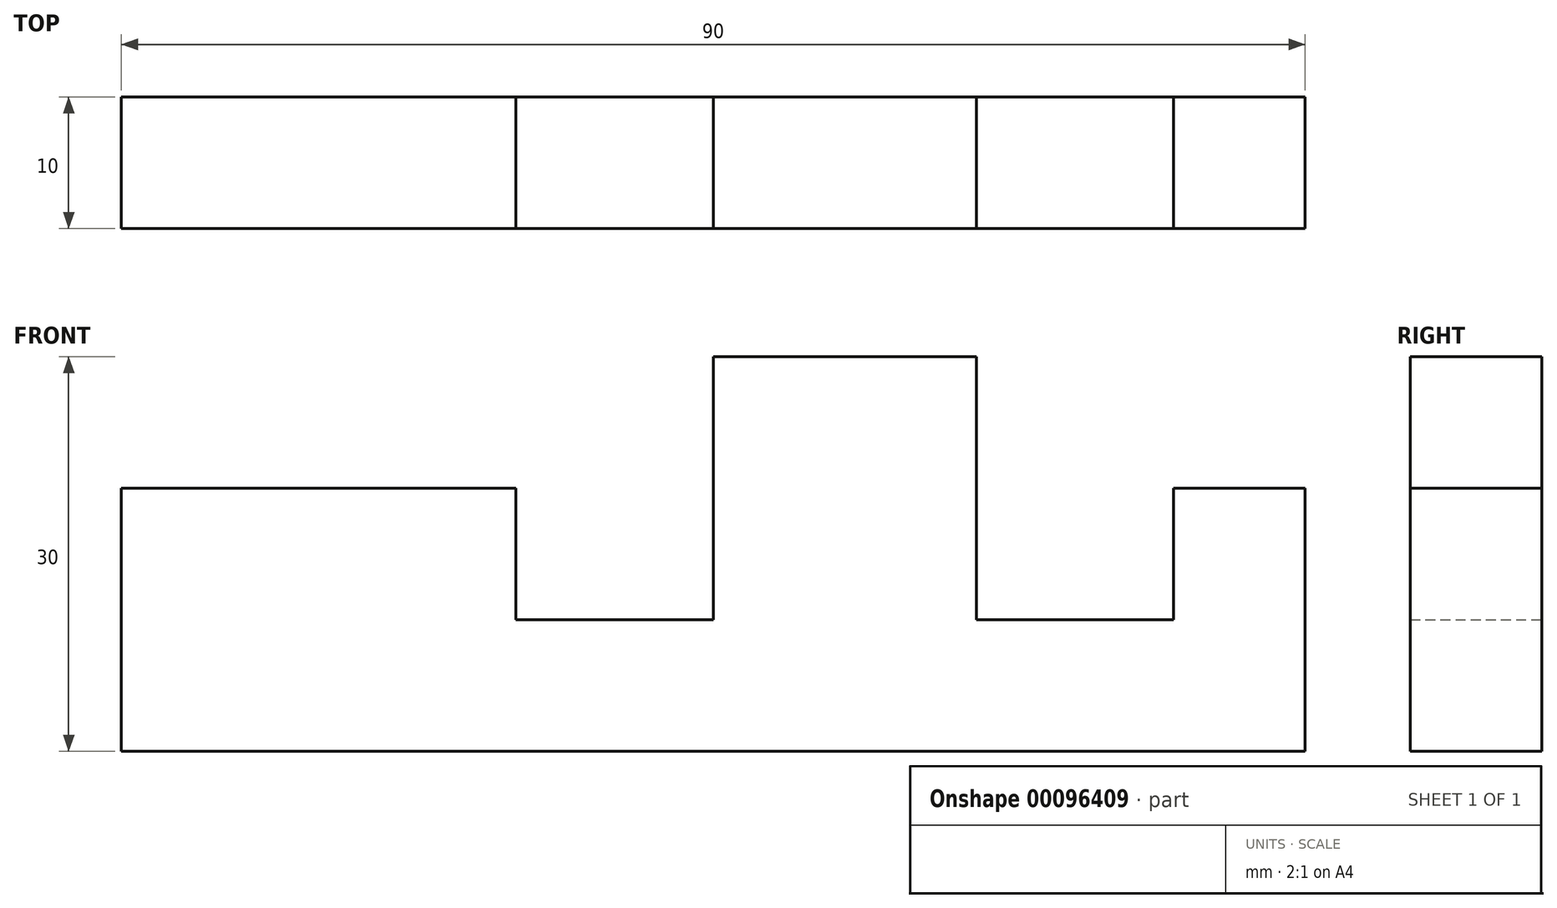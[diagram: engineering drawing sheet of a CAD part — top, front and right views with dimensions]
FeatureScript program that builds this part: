
annotation { "Feature Type Name" : "Feature", "Feature Type Description" : "" }
export const myFeature = defineFeature(function(context is Context, id is Id, definition is map)
    precondition{}
    {
        {
            var Q0;
            Q0=qCreatedBy(makeId("Front.planeOp"),FACE);
            var sketch = newSketch(context, id + "F0", { "sketchPlane" : qUnion([Q0])});
            skLineSegment(sketch, "E0", {"start": v(0, 0) * mm, "end": v(90, 0) * mm});
            skLineSegment(sketch, "E1", {"start": v(90, 0) * mm, "end": v(90, 20) * mm});
            skLineSegment(sketch, "E2", {"start": v(90, 20) * mm, "end": v(80, 20) * mm});
            skLineSegment(sketch, "E3", {"start": v(80, 20) * mm, "end": v(80, 10) * mm});
            skLineSegment(sketch, "E4", {"start": v(80, 10) * mm, "end": v(65, 10) * mm});
            skLineSegment(sketch, "E5", {"start": v(65, 10) * mm, "end": v(65, 30) * mm});
            skLineSegment(sketch, "E6", {"start": v(65, 30) * mm, "end": v(45, 30) * mm});
            skLineSegment(sketch, "E7", {"start": v(45, 30) * mm, "end": v(45, 10) * mm});
            skLineSegment(sketch, "E8", {"start": v(45, 10) * mm, "end": v(30, 10) * mm});
            skLineSegment(sketch, "E9", {"start": v(30, 10) * mm, "end": v(30, 20) * mm});
            skLineSegment(sketch, "E10", {"start": v(30, 20) * mm, "end": v(0, 20) * mm});
            skLineSegment(sketch, "E11", {"start": v(0, 20) * mm, "end": v(0, 0) * mm});
            skLineSegment(sketch, "E12", {"start": v(30, 20) * mm, "end": v(80, 20) * mm, "construction": true});
            skPoint(sketch, "E13.endSnap0", {"position": v(90, 10) * mm});
            skLineSegment(sketch, "E14", {"start": v(0, 10) * mm, "end": v(45, 10) * mm, "construction": true});
            skLineSegment(sketch, "E15", {"start": v(45, 10) * mm, "end": v(65, 10) * mm, "construction": true});
            skLineSegment(sketch, "E16", {"start": v(80, 10) * mm, "end": v(90, 10) * mm, "construction": true});
            skSolve(sketch);
        }
        {
            var Q0;
            Q0=makeQuery(id+"F0.imprint","IMPRINT",FACE,{"disambiguationData":[TD([[makeQuery(id+"F0.imprint","IMPRINT",EDGE,{"derivedFrom":sQuery(id+"F0.wireOp",EDGE,"E0")}),1.0]])]});
            extrude(context, id + "F1", {"entities" : qUnion([Q0]), "depth" : 10 * mm});
        }
    });
